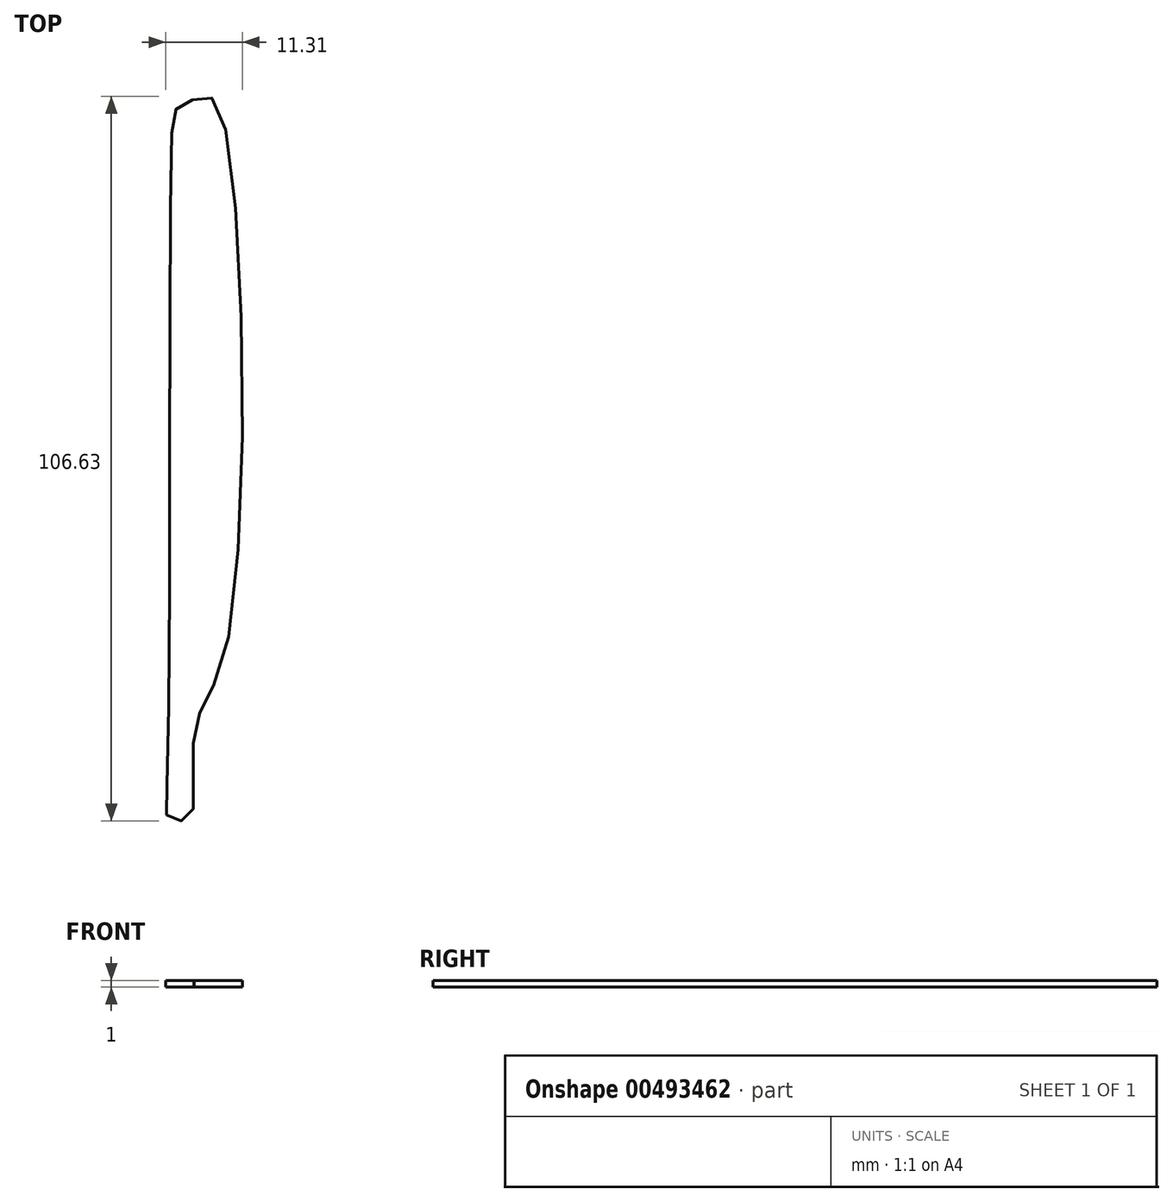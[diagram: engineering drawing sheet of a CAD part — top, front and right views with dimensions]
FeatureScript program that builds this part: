
annotation { "Feature Type Name" : "Feature", "Feature Type Description" : "" }
export const myFeature = defineFeature(function(context is Context, id is Id, definition is map)
    precondition{}
    {
        {
            var Q0;
            Q0=qCreatedBy(makeId("Top.planeOp"),FACE);
            var sketch = newSketch(context, id + "F0", { "sketchPlane" : qUnion([Q0])});
            skFitSpline(sketch, "E0", {"points": [v(-46.7, -48.93) * mm, v(-45.97, 47.94) * mm, v(-44.98, 50.9) * mm, v(-41.53, 52.38) * mm, v(-38.82, 50.4) * mm, v(-37.83, -28.22) * mm, v(-42.27, -39.31) * mm, v(-42.76, -49.17) * mm, v(-43.5, -53.86) * mm, v(-46.21, -53.86) * mm, v(-46.7, -48.93) * mm]});
            skSolve(sketch);
        }
        {
            var Q0;
            Q0=makeQuery(id+"F0.imprint","IMPRINT",FACE,{"disambiguationData":[TD([[makeQuery(id+"F0.imprint","IMPRINT",EDGE,{"derivedFrom":sQuery(id+"F0.wireOp",EDGE,"E0")}),-1.0]])]});
            extrude(context, id + "F1", {"entities" : qUnion([Q0]), "depth" : 1 * mm});
        }
    });
